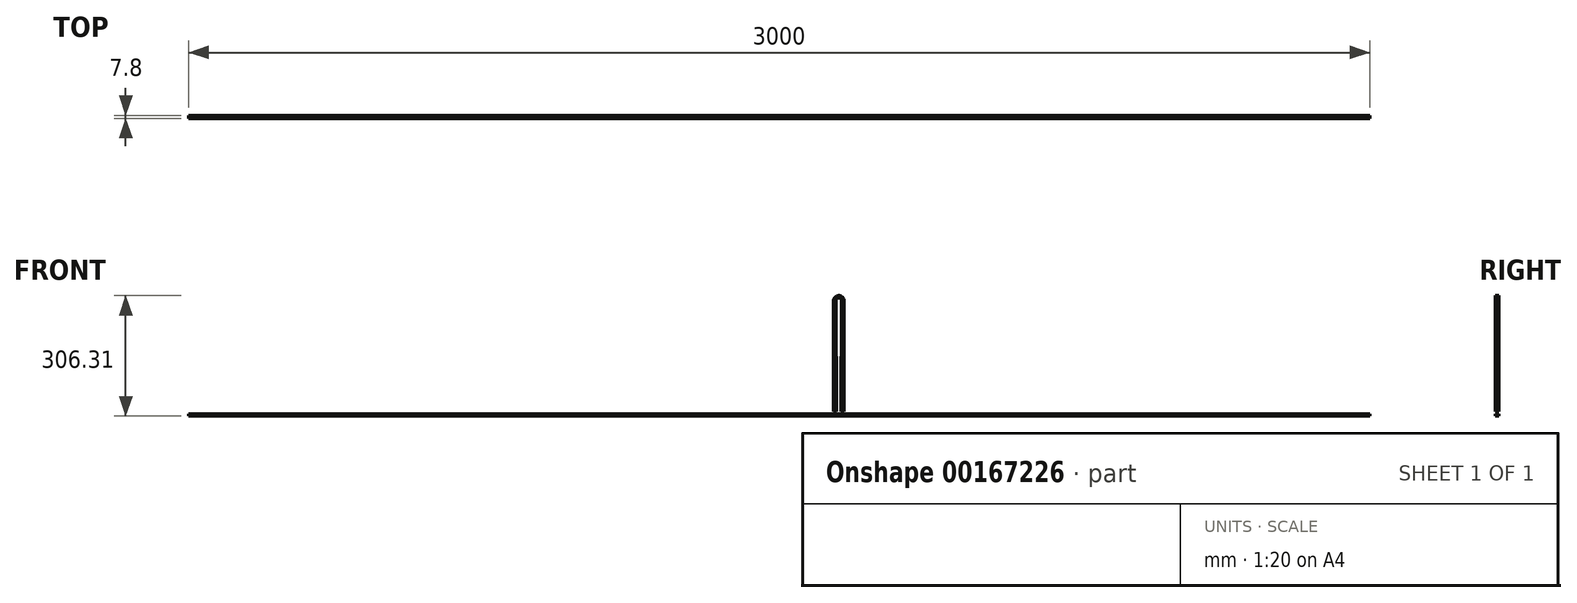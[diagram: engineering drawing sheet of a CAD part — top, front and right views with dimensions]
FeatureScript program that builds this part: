
annotation { "Feature Type Name" : "Feature", "Feature Type Description" : "" }
export const myFeature = defineFeature(function(context is Context, id is Id, definition is map)
    precondition{}
    {
        {
            var Q0;
            Q0=qCreatedBy(makeId("Front.planeOp"),FACE);
            var sketch = newSketch(context, id + "F0", { "sketchPlane" : qUnion([Q0])});
            skCircle(sketch, "E0.cCircle", {"center": v(0, 0) * mm, "radius": 10.27 * mm, "construction": true});
            skLineSegment(sketch, "E0.0", {"start": v(0, 10.27) * mm, "end": v(6.04, 8.31) * mm, "construction": true});
            skLineSegment(sketch, "E0.1", {"start": v(6.04, 8.31) * mm, "end": v(9.77, 3.18) * mm, "construction": true});
            skLineSegment(sketch, "E0.2", {"start": v(9.77, 3.18) * mm, "end": v(9.77, -3.17) * mm, "construction": true});
            skLineSegment(sketch, "E0.3", {"start": v(9.77, -3.17) * mm, "end": v(6.04, -8.31) * mm, "construction": true});
            skLineSegment(sketch, "E0.4", {"start": v(6.04, -8.31) * mm, "end": v(0, -10.27) * mm, "construction": true});
            skLineSegment(sketch, "E0.5", {"start": v(0, -10.27) * mm, "end": v(-6.04, -8.31) * mm, "construction": true});
            skLineSegment(sketch, "E0.6", {"start": v(-6.04, -8.31) * mm, "end": v(-9.77, -3.18) * mm, "construction": true});
            skLineSegment(sketch, "E0.7", {"start": v(-9.77, -3.18) * mm, "end": v(-9.77, 3.17) * mm, "construction": true});
            skLineSegment(sketch, "E0.8", {"start": v(-9.77, 3.17) * mm, "end": v(-6.04, 8.31) * mm, "construction": true});
            skLineSegment(sketch, "E0.9", {"start": v(-6.04, 8.31) * mm, "end": v(0, 10.27) * mm, "construction": true});
            skCircle(sketch, "E1", {"center": v(0, 10.27) * mm, "radius": 2.93 * mm, "construction": true});
            skCircle(sketch, "E2", {"center": v(0, 0) * mm, "radius": 7.35 * mm});
            skCircle(sketch, "E3", {"center": v(0, 0) * mm, "radius": 13.2 * mm});
            skLineSegment(sketch, "E4", {"start": v(-13.2, 0) * mm, "end": v(-13.2, -281) * mm});
            skLineSegment(sketch, "E5", {"start": v(-13.2, -281) * mm, "end": v(-6.04, -281) * mm});
            skLineSegment(sketch, "E6", {"start": v(-6.04, -281) * mm, "end": v(-7.35, 0) * mm});
            skLineSegment(sketch, "E7", {"start": v(0, 0) * mm, "end": v(0, -104.03) * mm, "construction": true});
            skLineSegment(sketch, "E8.MirrorCS", {"start": v(6.04, -281) * mm, "end": v(7.35, 0) * mm});
            skLineSegment(sketch, "E9.MirrorCS", {"start": v(13.2, 0) * mm, "end": v(13.2, -281) * mm});
            skLineSegment(sketch, "E10.MirrorCS", {"start": v(13.2, -281) * mm, "end": v(6.04, -281) * mm});
            skSolve(sketch);
        }
        {
            var Q0;
            {var subQ4=sQuery(id+"F0.wireOp",EDGE,"E2");var subQ7=sQuery(id+"F0.wireOp",EDGE,"E6");var subQ10=makeQuery(id+"F0.imprint","INTERSECT",VERTEX,{"disambiguationData":[OD(0.0)],"derivedFrom":[subQ4,subQ7]});Q0=makeQuery(id+"F0.imprint","IMPRINT",FACE,{"disambiguationData":[TD([[makeQuery(id+"F0.imprint","IMPRINT",EDGE,{"disambiguationData":[TD([[subQ10,1.0]])],"derivedFrom":subQ4}),-1.0]])]});}
            var Q1;
            {var subQ0=sQuery(id+"F0.wireOp",EDGE,"E4");Q1=makeQuery(id+"F0.imprint","IMPRINT",FACE,{"disambiguationData":[TD([[makeQuery(id+"F0.imprint","IMPRINT",EDGE,{"derivedFrom":subQ0}),1.0]])]});}
            var Q2;
            {var subQ0=sQuery(id+"F0.wireOp",EDGE,"E9.MirrorCS");Q2=makeQuery(id+"F0.imprint","IMPRINT",FACE,{"disambiguationData":[TD([[makeQuery(id+"F0.imprint","IMPRINT",EDGE,{"derivedFrom":subQ0}),-1.0]])]});}
            extrude(context, id + "F1", {"entities" : qUnion([Q0, Q1, Q2]), "depth" : 7.8 * mm, "symmetric" : true});
        }
        {
            var Q0;
            Q0=qCreatedBy(makeId("Front.planeOp"),FACE);
            var sketch = newSketch(context, id + "F2", { "sketchPlane" : qUnion([Q0])});
            skLineSegment(sketch, "E11.bottom", {"start": v(1348.6, -287.26) * mm, "end": v(-1651.4, -287.26) * mm});
            skLineSegment(sketch, "E11.top", {"start": v(1348.6, -293.1) * mm, "end": v(-1651.4, -293.1) * mm});
            skLineSegment(sketch, "E11.left", {"start": v(1348.6, -287.26) * mm, "end": v(1348.6, -293.1) * mm});
            skLineSegment(sketch, "E11.right", {"start": v(-1651.4, -287.26) * mm, "end": v(-1651.4, -293.1) * mm});
            skSolve(sketch);
        }
        {
            var Q0;
            Q0=makeQuery(id+"F2.imprint","IMPRINT",FACE,{"disambiguationData":[TD([[makeQuery(id+"F2.imprint","IMPRINT",EDGE,{"derivedFrom":sQuery(id+"F2.wireOp",EDGE,"E11.bottom")}),1.0]])]});
            extrude(context, id + "F3", {"entities" : qUnion([Q0]), "depth" : 7.8 * mm, "symmetric" : true});
        }
    });
